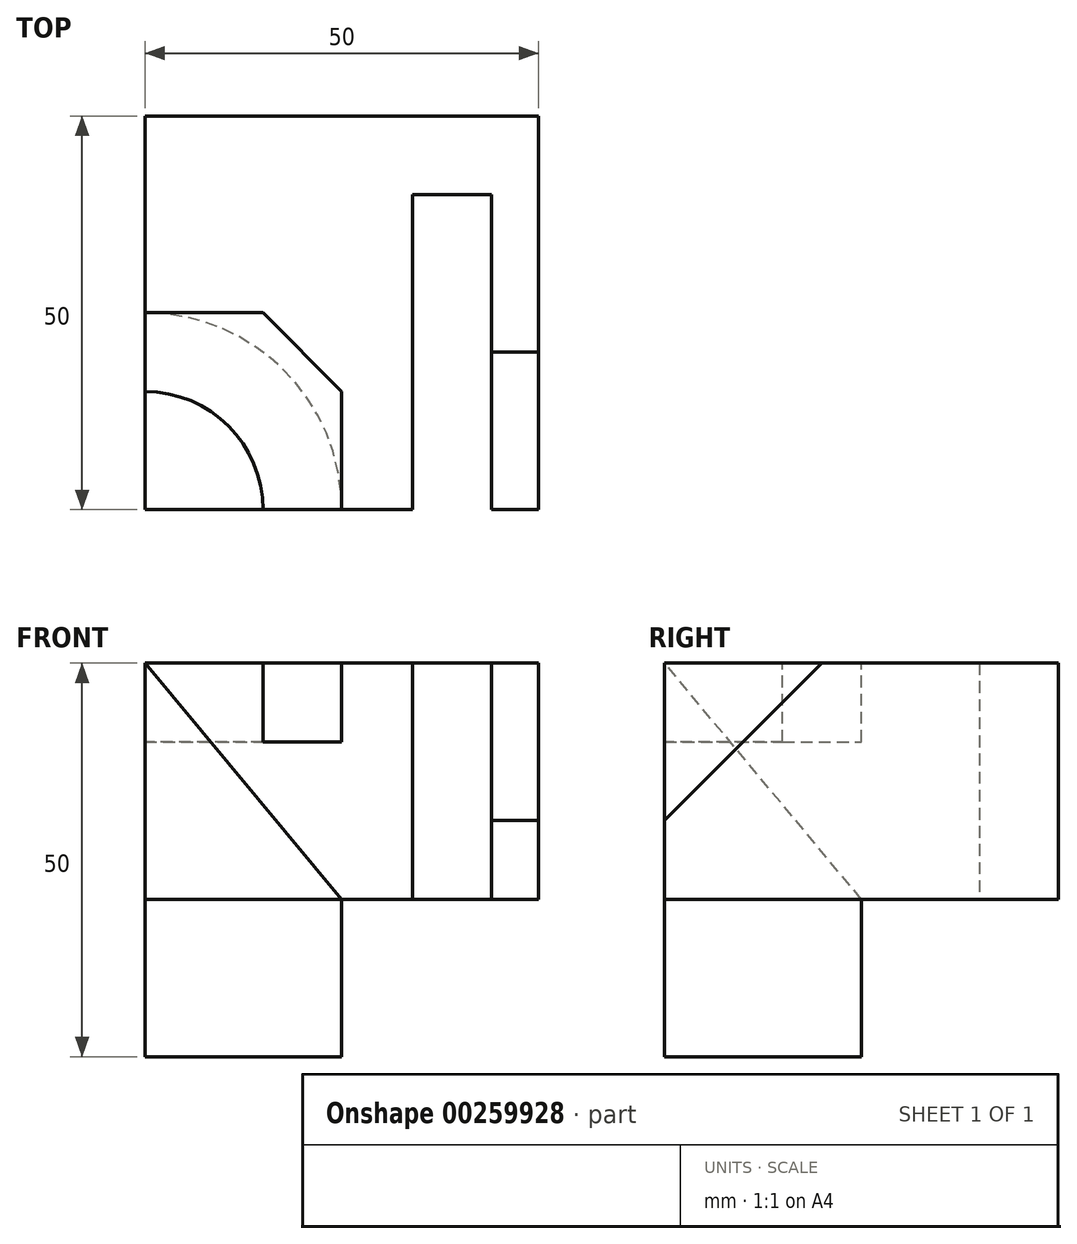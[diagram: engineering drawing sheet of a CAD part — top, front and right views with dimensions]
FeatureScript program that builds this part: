
annotation { "Feature Type Name" : "Feature", "Feature Type Description" : "" }
export const myFeature = defineFeature(function(context is Context, id is Id, definition is map)
    precondition{}
    {
        {
            var Q0;
            Q0=qCreatedBy(makeId("Top.planeOp"),FACE);
            var sketch = newSketch(context, id + "F0", { "sketchPlane" : qUnion([Q0])});
            skLineSegment(sketch, "E0.bottom", {"start": v(0, 0) * mm, "end": v(50, 0) * mm});
            skLineSegment(sketch, "E0.top", {"start": v(0, 50) * mm, "end": v(50, 50) * mm});
            skLineSegment(sketch, "E0.left", {"start": v(0, 0) * mm, "end": v(0, 50) * mm});
            skLineSegment(sketch, "E0.right", {"start": v(50, 0) * mm, "end": v(50, 50) * mm});
            skSolve(sketch);
        }
        {
            var Q0;
            Q0=qSketchRegion(id+"F0",true);
            extrude(context, id + "F1", {"entities" : qUnion([Q0]), "depth" : 50 * mm});
        }
        {
            var Q0;
            Q0=makeQuery(id+"F1.opExtrude","SWEPT_FACE",FACE,{"disambiguationData":[OSD([sQuery(id+"F0.wireOp",EDGE,"E0.bottom")])]});
            var sketch = newSketch(context, id + "F2", { "sketchPlane" : qUnion([Q0])});
            skLineSegment(sketch, "E1.bottom", {"start": v(44, 50) * mm, "end": v(34, 50) * mm});
            skLineSegment(sketch, "E1.top", {"start": v(44, 10) * mm, "end": v(34, 10) * mm});
            skLineSegment(sketch, "E1.left", {"start": v(44, 50) * mm, "end": v(44, 10) * mm});
            skLineSegment(sketch, "E1.right", {"start": v(34, 50) * mm, "end": v(34, 10) * mm});
            skSolve(sketch);
        }
        {
            var Q0;
            Q0=qSketchRegion(id+"F2",true);
            extrude(context, id + "F3", {"entities" : qUnion([Q0]), "operationType" : NewBodyOperationType.REMOVE, "oppositeDirection" : true, "depth" : 40 * mm});
        }
        {
            var Q0;
            Q0=makeQuery(id+"F3.boolean.opBoolean","COPY",EDGE,{"derivedFrom":makeQuery(id+"F3.opExtrude","CAP_EDGE",EDGE,{"disambiguationData":[OSD([sQuery(id+"F2.wireOp",EDGE,"E1.top")])],"isStart":false})});
            fillet(context, id + "F4", {"entities" : qUnion([Q0]), "radius" : 10 * mm, "tangentPropagation" : true, "allowEdgeOverflow" : false});
        }
        {
            var Q0;
            Q0=makeQuery(id+"F1.opExtrude","SWEPT_FACE",FACE,{"disambiguationData":[OSD([sQuery(id+"F0.wireOp",EDGE,"E0.bottom")])]});
            var sketch = newSketch(context, id + "F5", { "sketchPlane" : qUnion([Q0])});
            skLineSegment(sketch, "E2", {"start": v(0, 50) * mm, "end": v(25, 20) * mm});
            skLineSegment(sketch, "E3", {"start": v(25, 20) * mm, "end": v(25, 0) * mm});
            skLineSegment(sketch, "E4", {"start": v(25, 0) * mm, "end": v(0, 0) * mm});
            skLineSegment(sketch, "E5", {"start": v(0, 0) * mm, "end": v(0, 50) * mm});
            skSolve(sketch);
        }
        {
            var Q0;
            Q0=makeQuery(id+"F1.opExtrude","CAP_FACE",FACE,{"disambiguationData":[OSD([sQuery(id+"F0.wireOp",EDGE,"E0.bottom"),sQuery(id+"F0.wireOp",EDGE,"E0.top"),sQuery(id+"F0.wireOp",EDGE,"E0.left"),sQuery(id+"F0.wireOp",EDGE,"E0.right")])],"isStart":false});
            var sketch = newSketch(context, id + "F6", { "sketchPlane" : qUnion([Q0])});
            skArc(sketch, "E6", {"start": v(15, 0) * mm, "mid": v(10.6, 10.6) * mm, "end": v(0, 15) * mm});
            skLineSegment(sketch, "E7", {"start": v(0, 15) * mm, "end": v(0, 25) * mm});
            skLineSegment(sketch, "E8", {"start": v(0, 25) * mm, "end": v(25, 25) * mm});
            skLineSegment(sketch, "E9", {"start": v(25, 25) * mm, "end": v(25, 0) * mm});
            skLineSegment(sketch, "E10", {"start": v(25, 0) * mm, "end": v(15, 0) * mm});
            skSolve(sketch);
        }
        {
            var Q0;
            Q0=makeQuery(id+"F6.imprint","IMPRINT",FACE,{"disambiguationData":[TD([[makeQuery(id+"F6.imprint","IMPRINT",EDGE,{"derivedFrom":sQuery(id+"F6.wireOp",EDGE,"E6")}),-1.0]])]});
            extrude(context, id + "F7", {"entities" : qUnion([Q0]), "operationType" : NewBodyOperationType.REMOVE, "oppositeDirection" : true, "depth" : 10 * mm});
        }
        {
            var Q0;
            Q0=makeQuery(id+"F7.boolean.opBoolean","COPY",EDGE,{"derivedFrom":makeQuery(id+"F7.opExtrude","SWEPT_EDGE",EDGE,{"disambiguationData":[OSD([sQuery(id+"F6.wireOp",EDGE,"E8"),sQuery(id+"F6.wireOp",EDGE,"E9")])]})});
            chamfer(context, id + "F8", {"entities" : qUnion([Q0]), "width" : 10 * mm, "tangentPropagation" : true});
        }
        {
            var Q0;
            {var subQ0=sQuery(id+"F0.wireOp",EDGE,"E0.bottom");var subQ1=sQuery(id+"F0.wireOp",EDGE,"E0.right");Q0=makeQuery(id+"F3.boolean.opBoolean","SPLIT",EDGE,{"disambiguationData":[TD([makeQuery(id+"F1.opExtrude","SWEPT_FACE",FACE,{"disambiguationData":[OSD([subQ1])]})])],"derivedFrom":makeQuery(id+"F1.opExtrude","CAP_EDGE",EDGE,{"disambiguationData":[OSD([subQ0])],"isStart":false})});}
            chamfer(context, id + "F9", {"entities" : qUnion([Q0]), "width" : 20 * mm, "tangentPropagation" : true});
        }
        {
            var Q0;
            Q0=makeQuery(id+"F1.opExtrude","CAP_FACE",FACE,{"disambiguationData":[OSD([sQuery(id+"F0.wireOp",EDGE,"E0.bottom"),sQuery(id+"F0.wireOp",EDGE,"E0.top"),sQuery(id+"F0.wireOp",EDGE,"E0.left"),sQuery(id+"F0.wireOp",EDGE,"E0.right")])],"isStart":true});
            var sketch = newSketch(context, id + "F10", { "sketchPlane" : qUnion([Q0])});
            skArc(sketch, "E11", {"start": v(25, 0) * mm, "mid": v(17.68, -17.68) * mm, "end": v(0, -25) * mm});
            skLineSegment(sketch, "E12", {"start": v(0, -25) * mm, "end": v(0, 0) * mm});
            skLineSegment(sketch, "E13", {"start": v(0, 0) * mm, "end": v(25, 0) * mm});
            skSolve(sketch);
        }
        {
            var Q0;
            Q0=makeQuery(id+"F10.imprint","IMPRINT",FACE,{"disambiguationData":[TD([[makeQuery(id+"F10.imprint","IMPRINT",EDGE,{"derivedFrom":sQuery(id+"F10.wireOp",EDGE,"E11")}),-1.0]])]});
            cPlane(context, id + "F11", {"entities" : qUnion([Q0]), "cplaneType" : CPlaneType.OFFSET, "offset" : 20 * mm, "oppositeDirection" : true, "width" : 150 * mm, "height" : 150 * mm});
        }
        {
            var Q0;
            Q0=qCreatedBy(id+"F11.planeOp",FACE);
            var sketch = newSketch(context, id + "F12", { "sketchPlane" : qUnion([Q0])});
            skArc(sketch, "E14.0.0", {"start": v(0, -25) * mm, "mid": v(17.68, -17.68) * mm, "end": v(25, 0) * mm});
            skLineSegment(sketch, "E14.0.1", {"start": v(25, 0) * mm, "end": v(0, 0) * mm});
            skLineSegment(sketch, "E14.0.2", {"start": v(0, 0) * mm, "end": v(0, -25) * mm});
            skSolve(sketch);
        }
        {
            var Q0;
            Q0=makeQuery(id+"F10.imprint","IMPRINT",FACE,{"disambiguationData":[TD([[makeQuery(id+"F10.imprint","IMPRINT",EDGE,{"derivedFrom":sQuery(id+"F10.wireOp",EDGE,"E11")}),-1.0]])]});
            var Q1;
            Q1=qCreatedBy(id+"F11.planeOp",FACE);
            extrude(context, id + "F13", {"entities" : qUnion([Q0]), "operationType" : NewBodyOperationType.REMOVE, "endBound" : BoundingType.UP_TO_SURFACE, "oppositeDirection" : true, "depth" : 25 * mm, "endBoundEntityFace" : qUnion([Q1]), "offsetDistance" : 25 * mm});
        }
        {
            var Q1;
            Q1 = qSketchRegion(id + "F12", true);
            var Q2;
            Q2=sQuery(id+"F5.wireOp",VERTEX,"E5.end");
            loft(context, id + "F14", {"operationType" : NewBodyOperationType.REMOVE, "sheetProfilesArray" : [{ "sheetProfileEntities" : qUnion([Q1]) }, { "sheetProfileEntities" : qUnion([Q2]) }]});
        }
    });
